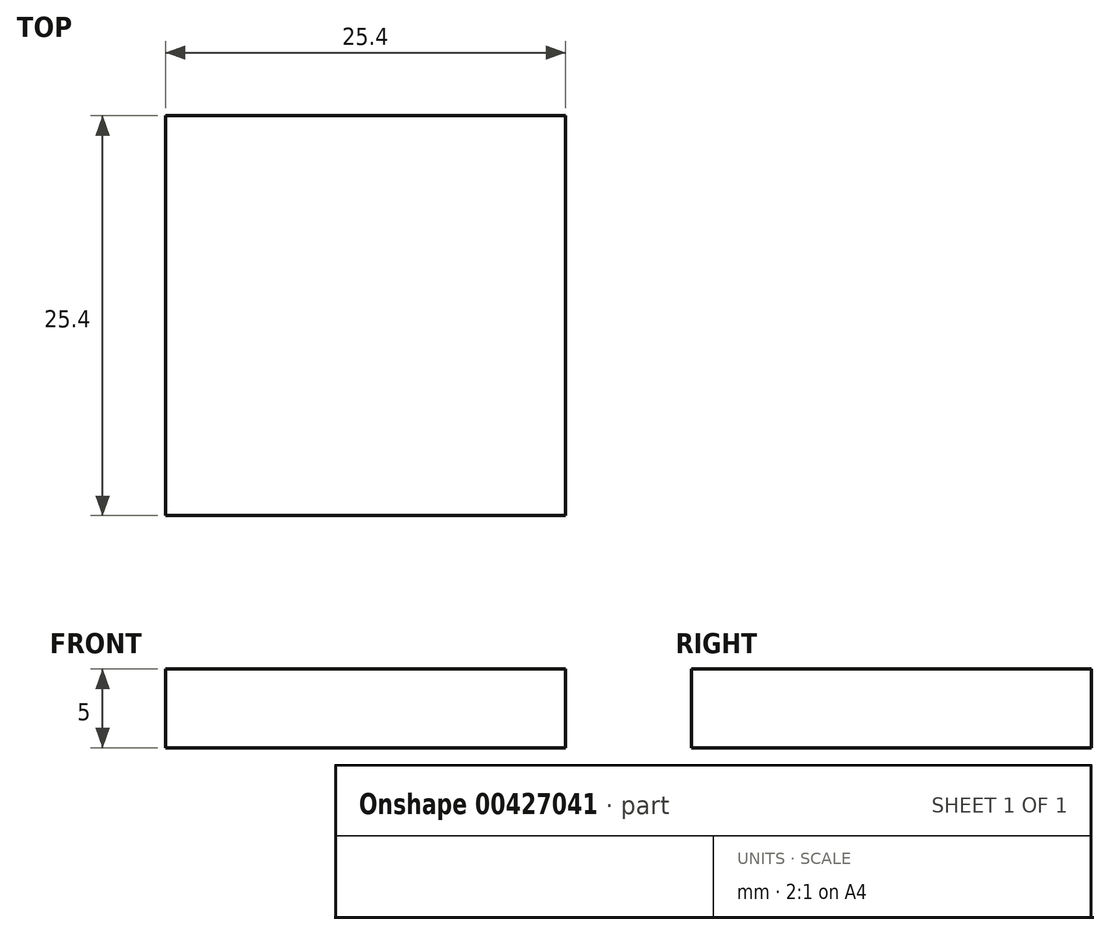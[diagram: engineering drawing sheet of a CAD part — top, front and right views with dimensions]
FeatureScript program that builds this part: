
annotation { "Feature Type Name" : "Feature", "Feature Type Description" : "" }
export const myFeature = defineFeature(function(context is Context, id is Id, definition is map)
    precondition{}
    {
        {
            var Q0;
            Q0=qCreatedBy(makeId("Top.planeOp"),FACE);
            var sketch = newSketch(context, id + "F0", { "sketchPlane" : qUnion([Q0])});
            skLineSegment(sketch, "E0.bottom", {"start": v(0, 0) * mm, "end": v(25.4, 0) * mm});
            skLineSegment(sketch, "E0.top", {"start": v(0, 25.4) * mm, "end": v(25.4, 25.4) * mm});
            skLineSegment(sketch, "E0.left", {"start": v(0, 0) * mm, "end": v(0, 25.4) * mm});
            skLineSegment(sketch, "E0.right", {"start": v(25.4, 0) * mm, "end": v(25.4, 25.4) * mm});
            skSolve(sketch);
        }
        {
            var Q0;
            Q0=makeQuery(id+"F0.imprint","IMPRINT",FACE,{"disambiguationData":[TD([[makeQuery(id+"F0.imprint","IMPRINT",EDGE,{"derivedFrom":sQuery(id+"F0.wireOp",EDGE,"E0.bottom")}),1.0]])]});
            extrude(context, id + "F1", {"entities" : qUnion([Q0]), "depth" : 5 * mm});
        }
    });
